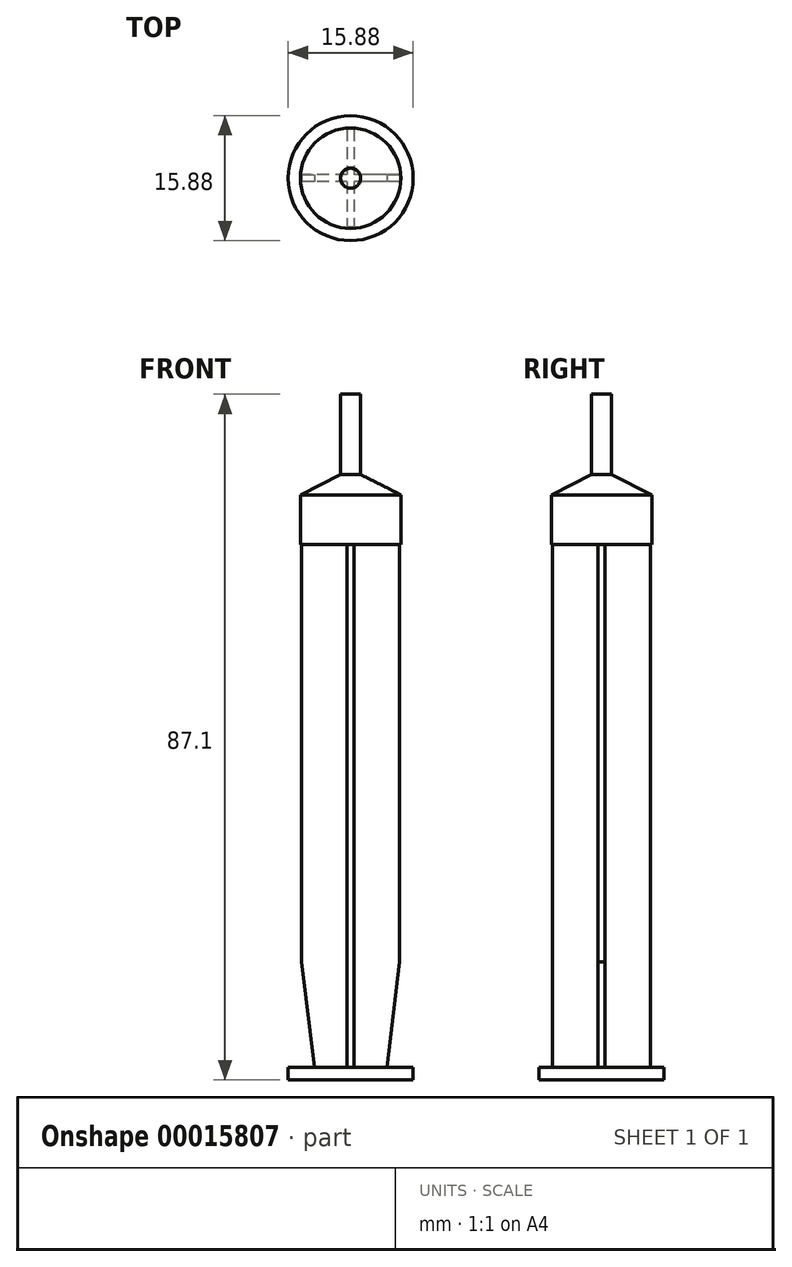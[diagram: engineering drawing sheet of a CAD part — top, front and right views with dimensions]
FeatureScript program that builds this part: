
annotation { "Feature Type Name" : "Feature", "Feature Type Description" : "" }
export const myFeature = defineFeature(function(context is Context, id is Id, definition is map)
    precondition{}
    {
        {
            var Q0;
            Q0=qCreatedBy(makeId("Top.planeOp"),FACE);
            var sketch = newSketch(context, id + "F0", { "sketchPlane" : qUnion([Q0])});
            skCircle(sketch, "E0", {"center": v(0, 0) * mm, "radius": 7.94 * mm});
            skSolve(sketch);
        }
        {
            var Q0;
            Q0 = qSketchRegion(id + "F0", true);
            extrude(context, id + "F1", {"entities" : qUnion([Q0]), "depth" : 1.57 * mm});
        }
        {
            var Q0;
            Q0=makeQuery(id+"F1.opExtrude","CAP_FACE",FACE,{"disambiguationData":[OSD([sQuery(id+"F0.wireOp",EDGE,"E0")])],"isStart":false});
            var sketch = newSketch(context, id + "F2", { "sketchPlane" : qUnion([Q0])});
            skLineSegment(sketch, "E1.rect.bottom", {"start": v(6.22, 0.44) * mm, "end": v(-6.22, 0.44) * mm});
            skLineSegment(sketch, "E1.rect.top", {"start": v(6.22, -0.44) * mm, "end": v(-6.22, -0.44) * mm});
            skLineSegment(sketch, "E1.rect.left", {"start": v(6.22, 0.44) * mm, "end": v(6.22, -0.44) * mm});
            skLineSegment(sketch, "E1.rect.right", {"start": v(-6.22, 0.44) * mm, "end": v(-6.22, -0.44) * mm});
            skPoint(sketch, "E1.rect.middle", {"position": v(0, 0) * mm});
            skLineSegment(sketch, "E2.rect.bottom", {"start": v(0.44, 6.22) * mm, "end": v(-0.44, 6.22) * mm});
            skLineSegment(sketch, "E2.rect.top", {"start": v(0.44, -6.22) * mm, "end": v(-0.44, -6.22) * mm});
            skLineSegment(sketch, "E2.rect.left", {"start": v(0.44, 6.22) * mm, "end": v(0.44, -6.22) * mm});
            skLineSegment(sketch, "E2.rect.right", {"start": v(-0.44, 6.22) * mm, "end": v(-0.44, -6.22) * mm});
            skSolve(sketch);
        }
        {
            var Q0;
            Q0 = qSketchRegion(id + "F2", true);
            extrude(context, id + "F3", {"entities" : qUnion([Q0]), "operationType" : NewBodyOperationType.ADD, "depth" : 66.42 * mm});
        }
        {
            var Q0;
            Q0=makeQuery(id+"F3.opExtrude","CAP_FACE",FACE,{"disambiguationData":[OSD([sQuery(id+"F2.wireOp",EDGE,"E1.rect.bottom"),sQuery(id+"F2.wireOp",EDGE,"E1.rect.top"),sQuery(id+"F2.wireOp",EDGE,"E1.rect.left"),sQuery(id+"F2.wireOp",EDGE,"E1.rect.right"),sQuery(id+"F2.wireOp",EDGE,"E2.rect.bottom"),sQuery(id+"F2.wireOp",EDGE,"E2.rect.top"),sQuery(id+"F2.wireOp",EDGE,"E2.rect.left"),sQuery(id+"F2.wireOp",EDGE,"E2.rect.right")])],"isStart":false});
            var sketch = newSketch(context, id + "F4", { "sketchPlane" : qUnion([Q0])});
            skLineSegment(sketch, "E3", {"start": v(0.44, -0.44) * mm, "end": v(-0.44, 0.44) * mm});
            skCircle(sketch, "E4", {"center": v(0, 0) * mm, "radius": 6.38 * mm});
            skSolve(sketch);
        }
        {
            var Q0;
            Q0 = qSketchRegion(id + "F4", true);
            extrude(context, id + "F5", {"entities" : qUnion([Q0]), "operationType" : NewBodyOperationType.ADD, "depth" : 8.9 * mm});
        }
        {
            var Q0;
            Q0=makeQuery(id+"F5.opExtrude","CAP_EDGE",EDGE,{"disambiguationData":[OSD([sQuery(id+"F4.wireOp",EDGE,"E4")])],"isStart":false});
            chamfer(context, id + "F6", {"entities" : qUnion([Q0]), "chamferType" : ChamferType.TWO_OFFSETS, "width1" : 5.1 * mm, "oppositeDirection" : false, "width2" : 2.57 * mm, "tangentPropagation" : true});
        }
        {
            var Q0;
            Q0=makeQuery(id+"F5.opExtrude","CAP_FACE",FACE,{"disambiguationData":[OSD([sQuery(id+"F4.wireOp",EDGE,"E4")])],"isStart":false});
            var sketch = newSketch(context, id + "F7", { "sketchPlane" : qUnion([Q0])});
            skCircle(sketch, "E5", {"center": v(0, 0) * mm, "radius": 1.27 * mm});
            skSolve(sketch);
        }
        {
            var Q0;
            Q0 = qSketchRegion(id + "F7", true);
            extrude(context, id + "F8", {"entities" : qUnion([Q0]), "operationType" : NewBodyOperationType.ADD, "depth" : 10.21 * mm});
        }
        {
            var Q0;
            {var subQ0=sQuery(id+"F2.wireOp",EDGE,"E1.rect.top");Q0=makeQuery(id+"F3.opExtrude","SWEPT_FACE",FACE,{"disambiguationData":[OSD([subQ0]),TDD([makeQuery(id+"F2.imprint","IMPRINT",EDGE,{"disambiguationData":[TD([[makeQuery(id+"F2.imprint","INTERSECT",VERTEX,{"derivedFrom":[subQ0,sQuery(id+"F2.wireOp",EDGE,"E1.rect.right")]}),1.0]])],"derivedFrom":subQ0})])]});}
            var sketch = newSketch(context, id + "F9", { "sketchPlane" : qUnion([Q0])});
            skLineSegment(sketch, "E6.bottom", {"start": v(-6.22, 1.57) * mm, "end": v(-4.61, 1.57) * mm});
            skLineSegment(sketch, "E6.top", {"start": v(-6.22, 14.96) * mm, "end": v(-4.61, 14.96) * mm, "construction": true});
            skLineSegment(sketch, "E6.left", {"start": v(-6.22, 1.57) * mm, "end": v(-6.22, 14.96) * mm});
            skLineSegment(sketch, "E6.right", {"start": v(-4.61, 1.57) * mm, "end": v(-4.61, 14.96) * mm, "construction": true});
            skLineSegment(sketch, "E7.bottom", {"start": v(4.61, 14.96) * mm, "end": v(6.22, 14.96) * mm, "construction": true});
            skLineSegment(sketch, "E7.top", {"start": v(4.61, 1.57) * mm, "end": v(6.22, 1.57) * mm});
            skLineSegment(sketch, "E7.left", {"start": v(4.61, 14.96) * mm, "end": v(4.61, 1.57) * mm, "construction": true});
            skLineSegment(sketch, "E7.right", {"start": v(6.22, 14.96) * mm, "end": v(6.22, 1.57) * mm});
            skLineSegment(sketch, "E8", {"start": v(6.22, 14.96) * mm, "end": v(4.61, 1.57) * mm});
            skLineSegment(sketch, "E9", {"start": v(-4.61, 1.57) * mm, "end": v(-6.22, 14.96) * mm});
            skSolve(sketch);
        }
        {
            var Q0;
            Q0 = qSketchRegion(id + "F9", true);
            var Q1;
            {var subQ0=sQuery(id+"F2.wireOp",EDGE,"E1.rect.bottom");Q1=makeQuery(id+"F3.opExtrude","SWEPT_FACE",FACE,{"disambiguationData":[OSD([subQ0]),TDD([makeQuery(id+"F2.imprint","IMPRINT",EDGE,{"disambiguationData":[TD([[makeQuery(id+"F2.imprint","INTERSECT",VERTEX,{"derivedFrom":[subQ0,sQuery(id+"F2.wireOp",EDGE,"E1.rect.left")]}),-1.0]])],"derivedFrom":subQ0})])]});}
            extrude(context, id + "F10", {"entities" : qUnion([Q0]), "operationType" : NewBodyOperationType.REMOVE, "endBound" : BoundingType.UP_TO_SURFACE, "oppositeDirection" : true, "endBoundEntityFace" : qUnion([Q1]), "depth" : 25.4 * mm});
        }
    });
